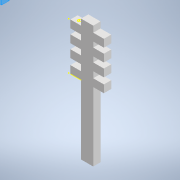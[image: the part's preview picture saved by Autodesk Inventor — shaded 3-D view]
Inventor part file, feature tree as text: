
AUTODESK INVENTOR PART (.ipt)
format: ipt  version: 2020 (Build 240168000, 168)  size: 145,408 bytes
history: native  units: in
note: dims shown in document units (in); Inventor stores cm internally (conversion verified against a paired STEP export)
features: reference x4, sketch x3, other x3, plane x1, extrude x1, projected_geometry x1
ambient origin geometry x8: Origin, YZ Plane, XZ Plane, XY Plane, X Axis, Y Axis, Z Axis, Center Point
bodies: Solid1 (feature_tree)
feature tree (13):
  plane  "Work Plane1"
  extrude  "Extrusion1"  Depth=0.689in
  sketch  "Sketch2"  dims[d2=0.689in]
  sketch  "Sketch3"  dims[d3=0.4921in d4=0.3937in d5=0.0in]
  sketch  "Sketch1"  dims[d0=7.874in d1=0.689in]
  reference  "Reference1"
  reference  "Reference2"
  projected_geometry  "Projected Loop1"
  reference  "Reference3"
  reference  "Reference4"
  other  "Assembly3.iam"
  other  "Part9 scaled:1"
  other  "Part9 scaled:2"
